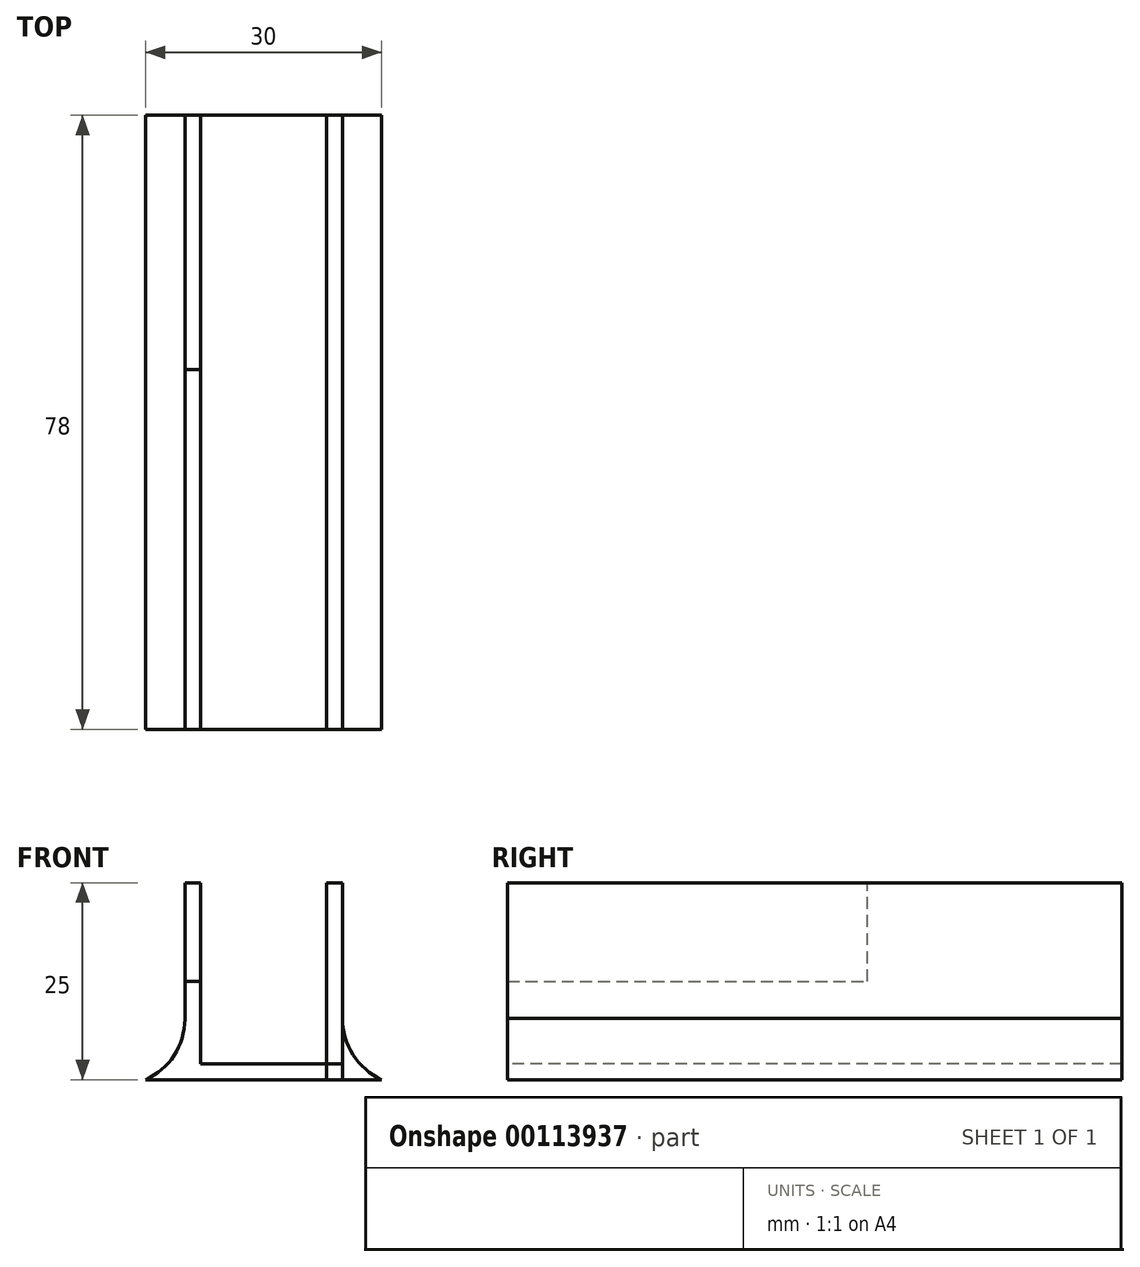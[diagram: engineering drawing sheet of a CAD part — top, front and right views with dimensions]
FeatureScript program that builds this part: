
annotation { "Feature Type Name" : "Feature", "Feature Type Description" : "" }
export const myFeature = defineFeature(function(context is Context, id is Id, definition is map)
    precondition{}
    {
        {
            var Q0;
            Q0=qCreatedBy(makeId("Top.planeOp"),FACE);
            var sketch = newSketch(context, id + "F0", { "sketchPlane" : qUnion([Q0])});
            skLineSegment(sketch, "E0.bottom", {"start": v(10, -39) * mm, "end": v(-10, -39) * mm});
            skLineSegment(sketch, "E0.top", {"start": v(10, 39) * mm, "end": v(-10, 39) * mm});
            skLineSegment(sketch, "E0.left", {"start": v(10, -39) * mm, "end": v(10, 39) * mm});
            skLineSegment(sketch, "E0.right", {"start": v(-10, -39) * mm, "end": v(-10, 39) * mm});
            skPoint(sketch, "E0.middle", {"position": v(0, 0) * mm});
            skLineSegment(sketch, "E1", {"start": v(-8, 39) * mm, "end": v(-8, -39) * mm});
            skLineSegment(sketch, "E2", {"start": v(8, 39) * mm, "end": v(8, -39) * mm});
            skSolve(sketch);
        }
        {
            var Q0;
            {var subQ0=sQuery(id+"F0.wireOp",EDGE,"E0.left");Q0=makeQuery(id+"F0.imprint","IMPRINT",FACE,{"disambiguationData":[TD([[makeQuery(id+"F0.imprint","IMPRINT",EDGE,{"derivedFrom":subQ0}),1.0]])]});}
            var Q1;
            {var subQ0=sQuery(id+"F0.wireOp",EDGE,"E0.right");Q1=makeQuery(id+"F0.imprint","IMPRINT",FACE,{"disambiguationData":[TD([[makeQuery(id+"F0.imprint","IMPRINT",EDGE,{"derivedFrom":subQ0}),-1.0]])]});}
            extrude(context, id + "F1", {"entities" : qUnion([Q0, Q1]), "depth" : 25 * mm});
        }
        {
            var Q0;
            Q0 = qSketchRegion(id + "F0", true);
            extrude(context, id + "F2", {"entities" : qUnion([Q0]), "depth" : 2 * mm});
        }
        {
            var Q0;
            Q0=makeQuery(id+"F1.opExtrude","SWEPT_FACE",FACE,{"disambiguationData":[OSD([sQuery(id+"F0.wireOp",EDGE,"E0.right")])]});
            var sketch = newSketch(context, id + "F3", { "sketchPlane" : qUnion([Q0])});
            skLineSegment(sketch, "E3", {"start": v(39, 12.5) * mm, "end": v(-6.69, 12.5) * mm});
            skPoint(sketch, "E3.endSnap0", {"position": v(39, 12.5) * mm});
            skLineSegment(sketch, "E4", {"start": v(-6.69, 12.5) * mm, "end": v(-6.69, 25) * mm});
            skLineSegment(sketch, "E5", {"start": v(-6.69, 25) * mm, "end": v(39, 25) * mm});
            skLineSegment(sketch, "E6", {"start": v(39, 25) * mm, "end": v(39, 12.5) * mm});
            skSolve(sketch);
        }
        {
            var Q0;
            Q0 = qSketchRegion(id + "F3", true);
            extrude(context, id + "F4", {"entities" : qUnion([Q0]), "operationType" : NewBodyOperationType.REMOVE, "oppositeDirection" : true, "depth" : 10 * mm});
        }
        {
            var Q0;
            {var subQ0=sQuery(id+"F0.wireOp",EDGE,"E0.top");Q0=makeQuery(id+"F1.opExtrude","SWEPT_FACE",FACE,{"disambiguationData":[OSD([subQ0]),TDD([makeQuery(id+"F0.imprint","IMPRINT",EDGE,{"disambiguationData":[TD([[makeQuery(id+"F0.imprint","INTERSECT",VERTEX,{"derivedFrom":[subQ0,sQuery(id+"F0.wireOp",EDGE,"E0.right")]}),1.0]])],"derivedFrom":subQ0})])]});}
            var sketch = newSketch(context, id + "F5", { "sketchPlane" : qUnion([Q0])});
            skLineSegment(sketch, "E7", {"start": v(15, 0) * mm, "end": v(10, 0) * mm});
            skLineSegment(sketch, "E8", {"start": v(10, 0) * mm, "end": v(10, 7.68) * mm});
            skArc(sketch, "E9", {"start": v(10, 7.68) * mm, "mid": v(11.36, 3.1) * mm, "end": v(15, 0) * mm});
            skSolve(sketch);
        }
        {
            var Q0;
            {var subQ0=sQuery(id+"F0.wireOp",EDGE,"E0.top");Q0=makeQuery(id+"F1.opExtrude","SWEPT_FACE",FACE,{"disambiguationData":[OSD([subQ0]),TDD([makeQuery(id+"F0.imprint","IMPRINT",EDGE,{"disambiguationData":[TD([[makeQuery(id+"F0.imprint","INTERSECT",VERTEX,{"derivedFrom":[subQ0,sQuery(id+"F0.wireOp",EDGE,"E0.left")]}),-1.0]])],"derivedFrom":subQ0})])]});}
            var sketch = newSketch(context, id + "F6", { "sketchPlane" : qUnion([Q0])});
            skLineSegment(sketch, "E10", {"start": v(-15, 0) * mm, "end": v(-10, 0) * mm});
            skLineSegment(sketch, "E11", {"start": v(-10, 0) * mm, "end": v(-10, 7.81) * mm});
            skArc(sketch, "E12", {"start": v(-15, 0) * mm, "mid": v(-11.36, 3.18) * mm, "end": v(-10, 7.81) * mm});
            skSolve(sketch);
        }
        {
            var Q0;
            Q0=makeQuery(id+"F6.imprint","IMPRINT",FACE,{"disambiguationData":[TD([[makeQuery(id+"F6.imprint","IMPRINT",EDGE,{"derivedFrom":sQuery(id+"F6.wireOp",EDGE,"2I9cgdt4-GrEv-YIkm-PLgU-ayQEVJ8jVxYN")}),1.0]])]});
            var Q1;
            Q1=makeQuery(id+"F6.imprint","IMPRINT",FACE,{"disambiguationData":[TD([[makeQuery(id+"F6.imprint","IMPRINT",EDGE,{"derivedFrom":sQuery(id+"F6.wireOp",EDGE,"E10")}),1.0]])]});
            extrude(context, id + "F7", {"entities" : qUnion([Q0, Q1]), "oppositeDirection" : true, "depth" : 78 * mm});
        }
        {
            var Q0;
            Q0=makeQuery(id+"F5.imprint","IMPRINT",FACE,{"disambiguationData":[TD([[makeQuery(id+"F5.imprint","IMPRINT",EDGE,{"derivedFrom":sQuery(id+"F5.wireOp",EDGE,"E7")}),-1.0]])]});
            extrude(context, id + "F8", {"entities" : qUnion([Q0]), "operationType" : NewBodyOperationType.ADD, "oppositeDirection" : true, "depth" : 78 * mm});
        }
    });
